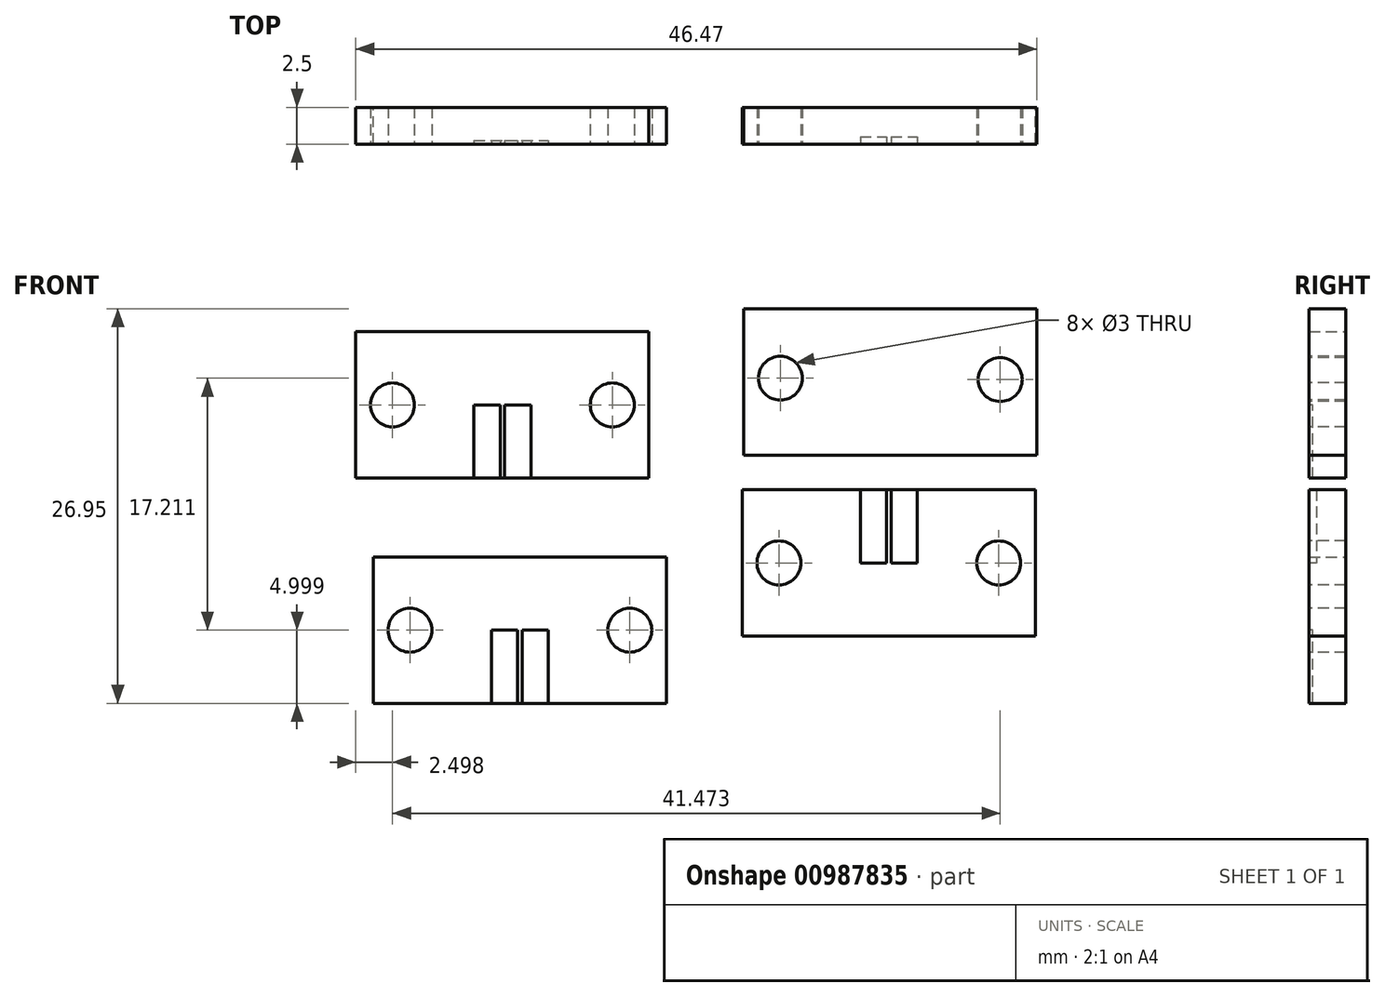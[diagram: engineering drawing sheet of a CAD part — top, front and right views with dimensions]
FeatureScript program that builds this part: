
annotation { "Feature Type Name" : "Feature", "Feature Type Description" : "" }
export const myFeature = defineFeature(function(context is Context, id is Id, definition is map)
    precondition{}
    {
        {
            var Q0;
            Q0=qCreatedBy(makeId("Front.planeOp"),FACE);
            var sketch = newSketch(context, id + "F0", { "sketchPlane" : qUnion([Q0])});
            skLineSegment(sketch, "E0.bottom", {"start": v(-45.26, 43.67) * mm, "end": v(-25.26, 43.67) * mm});
            skLineSegment(sketch, "E0.top", {"start": v(-45.26, 33.67) * mm, "end": v(-25.26, 33.67) * mm});
            skLineSegment(sketch, "E0.left", {"start": v(-45.26, 43.67) * mm, "end": v(-45.26, 33.67) * mm});
            skLineSegment(sketch, "E0.right", {"start": v(-25.26, 43.67) * mm, "end": v(-25.26, 33.67) * mm});
            skLineSegment(sketch, "E1.bottom", {"start": v(-45.36, 31.31) * mm, "end": v(-25.36, 31.31) * mm});
            skLineSegment(sketch, "E1.top", {"start": v(-45.36, 21.31) * mm, "end": v(-25.36, 21.31) * mm});
            skLineSegment(sketch, "E1.left", {"start": v(-45.36, 31.31) * mm, "end": v(-45.36, 21.31) * mm});
            skLineSegment(sketch, "E1.right", {"start": v(-25.36, 31.31) * mm, "end": v(-25.36, 21.31) * mm});
            skSolve(sketch);
        }
        {
            var Q0;
            Q0 = qSketchRegion(id + "F0", true);
            extrude(context, id + "F1", {"entities" : qUnion([Q0]), "depth" : 2.5 * mm, "offsetDistance" : 25 * mm});
        }
        {
            var Q0;
            Q0=makeQuery(id+"F1.opExtrude","CAP_FACE",FACE,{"disambiguationData":[OSD([sQuery(id+"F0.wireOp",EDGE,"E1.bottom"),sQuery(id+"F0.wireOp",EDGE,"E1.top"),sQuery(id+"F0.wireOp",EDGE,"E1.left"),sQuery(id+"F0.wireOp",EDGE,"E1.right")])],"isStart":false});
            var sketch = newSketch(context, id + "F2", { "sketchPlane" : qUnion([Q0])});
            skPoint(sketch, "E2", {"position": v(-35.36, 26.31) * mm});
            skLineSegment(sketch, "E3.bottom", {"start": v(-37.3, 31.9) * mm, "end": v(-35.5, 31.9) * mm});
            skLineSegment(sketch, "E3.top", {"start": v(-37.3, 26.31) * mm, "end": v(-35.5, 26.31) * mm});
            skLineSegment(sketch, "E3.left", {"start": v(-37.3, 31.9) * mm, "end": v(-37.3, 26.31) * mm});
            skLineSegment(sketch, "E3.right", {"start": v(-35.5, 31.9) * mm, "end": v(-35.5, 26.31) * mm});
            skLineSegment(sketch, "E4.bottom", {"start": v(-35.2, 32.08) * mm, "end": v(-33.4, 32.08) * mm});
            skLineSegment(sketch, "E4.top", {"start": v(-35.2, 26.31) * mm, "end": v(-33.4, 26.31) * mm});
            skLineSegment(sketch, "E4.left", {"start": v(-35.2, 32.08) * mm, "end": v(-35.2, 26.31) * mm});
            skLineSegment(sketch, "E4.right", {"start": v(-33.4, 32.08) * mm, "end": v(-33.4, 26.31) * mm});
            skSolve(sketch);
        }
        {
            var Q0;
            Q0 = qSketchRegion(id + "F2", true);
            extrude(context, id + "F3", {"entities" : qUnion([Q0]), "operationType" : NewBodyOperationType.REMOVE, "oppositeDirection" : true, "depth" : .5 * mm, "offsetDistance" : 25 * mm});
        }
        {
            var Q0;
            Q0=makeQuery(id+"F1.opExtrude","CAP_FACE",FACE,{"disambiguationData":[OSD([sQuery(id+"F0.wireOp",EDGE,"E1.bottom"),sQuery(id+"F0.wireOp",EDGE,"E1.top"),sQuery(id+"F0.wireOp",EDGE,"E1.left"),sQuery(id+"F0.wireOp",EDGE,"E1.right")])],"isStart":false});
            var sketch = newSketch(context, id + "F4", { "sketchPlane" : qUnion([Q0])});
            skPoint(sketch, "E5", {"position": v(-42.86, 26.31) * mm});
            skPoint(sketch, "E6", {"position": v(-27.86, 26.31) * mm});
            skCircle(sketch, "E7", {"center": v(-42.86, 26.31) * mm, "radius": 1.5 * mm});
            skCircle(sketch, "E8", {"center": v(-27.86, 26.31) * mm, "radius": 1.5 * mm});
            skSolve(sketch);
        }
        {
            var Q0;
            Q0 = qSketchRegion(id + "F4", true);
            extrude(context, id + "F5", {"entities" : qUnion([Q0]), "operationType" : NewBodyOperationType.REMOVE, "oppositeDirection" : true, "depth" : 3 * mm, "offsetDistance" : 25 * mm});
        }
        {
            var Q0;
            Q0=makeQuery(id+"F1.opExtrude","CAP_FACE",FACE,{"disambiguationData":[OSD([sQuery(id+"F0.wireOp",EDGE,"E0.bottom"),sQuery(id+"F0.wireOp",EDGE,"E0.top"),sQuery(id+"F0.wireOp",EDGE,"E0.left"),sQuery(id+"F0.wireOp",EDGE,"E0.right")])],"isStart":false});
            var sketch = newSketch(context, id + "F6", { "sketchPlane" : qUnion([Q0])});
            skPoint(sketch, "E9", {"position": v(-42.76, 38.93) * mm});
            skPoint(sketch, "E10", {"position": v(-27.76, 38.83) * mm});
            skCircle(sketch, "E11", {"center": v(-42.76, 38.93) * mm, "radius": 1.5 * mm});
            skCircle(sketch, "E12", {"center": v(-27.76, 38.83) * mm, "radius": 1.5 * mm});
            skSolve(sketch);
        }
        {
            var Q0;
            Q0 = qSketchRegion(id + "F6", true);
            extrude(context, id + "F7", {"entities" : qUnion([Q0]), "operationType" : NewBodyOperationType.REMOVE, "oppositeDirection" : true, "depth" : 3 * mm, "offsetDistance" : 25 * mm});
        }
        {
            var Q0;
            Q0=qCreatedBy(makeId("Front.planeOp"),FACE);
            var sketch = newSketch(context, id + "F8", { "sketchPlane" : qUnion([Q0])});
            skLineSegment(sketch, "E13.bottom", {"start": v(-71.73, 42.1) * mm, "end": v(-51.73, 42.1) * mm});
            skLineSegment(sketch, "E13.top", {"start": v(-71.73, 32.1) * mm, "end": v(-51.73, 32.1) * mm});
            skLineSegment(sketch, "E13.left", {"start": v(-71.73, 42.1) * mm, "end": v(-71.73, 32.1) * mm});
            skLineSegment(sketch, "E13.right", {"start": v(-51.73, 42.1) * mm, "end": v(-51.73, 32.1) * mm});
            skLineSegment(sketch, "E14.bottom", {"start": v(-70.54, 26.72) * mm, "end": v(-50.54, 26.72) * mm});
            skLineSegment(sketch, "E14.top", {"start": v(-70.54, 16.72) * mm, "end": v(-50.54, 16.72) * mm});
            skLineSegment(sketch, "E14.left", {"start": v(-70.54, 26.72) * mm, "end": v(-70.54, 16.72) * mm});
            skLineSegment(sketch, "E14.right", {"start": v(-50.54, 26.72) * mm, "end": v(-50.54, 16.72) * mm});
            skSolve(sketch);
        }
        {
            var Q0;
            Q0 = qSketchRegion(id + "F8", true);
            extrude(context, id + "F9", {"entities" : qUnion([Q0]), "depth" : 2.5 * mm, "offsetDistance" : 25 * mm});
        }
        {
            var Q0;
            Q0=makeQuery(id+"F9.opExtrude","CAP_FACE",FACE,{"disambiguationData":[OSD([sQuery(id+"F8.wireOp",EDGE,"E13.bottom"),sQuery(id+"F8.wireOp",EDGE,"E13.top"),sQuery(id+"F8.wireOp",EDGE,"E13.left"),sQuery(id+"F8.wireOp",EDGE,"E13.right")])],"isStart":false});
            var sketch = newSketch(context, id + "F10", { "sketchPlane" : qUnion([Q0])});
            skLineSegment(sketch, "E15.bottom", {"start": v(-63.68, 32.1) * mm, "end": v(-61.88, 32.1) * mm});
            skLineSegment(sketch, "E15.top", {"start": v(-63.68, 37.1) * mm, "end": v(-61.88, 37.1) * mm});
            skLineSegment(sketch, "E15.left", {"start": v(-63.68, 32.1) * mm, "end": v(-63.68, 37.1) * mm});
            skLineSegment(sketch, "E15.right", {"start": v(-61.88, 32.1) * mm, "end": v(-61.88, 37.1) * mm});
            skLineSegment(sketch, "E16.bottom", {"start": v(-59.78, 32.1) * mm, "end": v(-61.58, 32.1) * mm});
            skLineSegment(sketch, "E16.top", {"start": v(-59.78, 37.1) * mm, "end": v(-61.58, 37.1) * mm});
            skLineSegment(sketch, "E16.left", {"start": v(-59.78, 32.1) * mm, "end": v(-59.78, 37.1) * mm});
            skLineSegment(sketch, "E16.right", {"start": v(-61.58, 32.1) * mm, "end": v(-61.58, 37.1) * mm});
            skPoint(sketch, "E17", {"position": v(-61.73, 37.1) * mm});
            skSolve(sketch);
        }
        {
            var Q0;
            Q0 = qSketchRegion(id + "F10", true);
            extrude(context, id + "F11", {"entities" : qUnion([Q0]), "operationType" : NewBodyOperationType.REMOVE, "oppositeDirection" : true, "depth" : .25 * mm, "offsetDistance" : 25 * mm});
        }
        {
            var Q0;
            Q0=makeQuery(id+"F9.opExtrude","CAP_FACE",FACE,{"disambiguationData":[OSD([sQuery(id+"F8.wireOp",EDGE,"E14.bottom"),sQuery(id+"F8.wireOp",EDGE,"E14.top"),sQuery(id+"F8.wireOp",EDGE,"E14.left"),sQuery(id+"F8.wireOp",EDGE,"E14.right")])],"isStart":false});
            var sketch = newSketch(context, id + "F12", { "sketchPlane" : qUnion([Q0])});
            skLineSegment(sketch, "E18.bottom", {"start": v(-62.49, 16.72) * mm, "end": v(-60.69, 16.72) * mm});
            skLineSegment(sketch, "E18.top", {"start": v(-62.49, 21.72) * mm, "end": v(-60.69, 21.72) * mm});
            skLineSegment(sketch, "E18.left", {"start": v(-62.49, 16.72) * mm, "end": v(-62.49, 21.72) * mm});
            skLineSegment(sketch, "E18.right", {"start": v(-60.69, 16.72) * mm, "end": v(-60.69, 21.72) * mm});
            skLineSegment(sketch, "E19.bottom", {"start": v(-60.39, 16.72) * mm, "end": v(-58.59, 16.72) * mm});
            skLineSegment(sketch, "E19.top", {"start": v(-60.39, 21.72) * mm, "end": v(-58.59, 21.72) * mm});
            skLineSegment(sketch, "E19.left", {"start": v(-60.39, 16.72) * mm, "end": v(-60.39, 21.72) * mm});
            skLineSegment(sketch, "E19.right", {"start": v(-58.59, 16.72) * mm, "end": v(-58.59, 21.72) * mm});
            skPoint(sketch, "E20", {"position": v(-60.54, 21.72) * mm});
            skSolve(sketch);
        }
        {
            var Q0;
            Q0 = qSketchRegion(id + "F12", true);
            extrude(context, id + "F13", {"entities" : qUnion([Q0]), "operationType" : NewBodyOperationType.REMOVE, "oppositeDirection" : true, "depth" : .25 * mm, "offsetDistance" : 25 * mm});
        }
        {
            var Q0;
            Q0=makeQuery(id+"F9.opExtrude","CAP_FACE",FACE,{"disambiguationData":[OSD([sQuery(id+"F8.wireOp",EDGE,"E13.bottom"),sQuery(id+"F8.wireOp",EDGE,"E13.top"),sQuery(id+"F8.wireOp",EDGE,"E13.left"),sQuery(id+"F8.wireOp",EDGE,"E13.right")])],"isStart":false});
            var sketch = newSketch(context, id + "F14", { "sketchPlane" : qUnion([Q0])});
            skPoint(sketch, "E21", {"position": v(-69.23, 37.1) * mm});
            skPoint(sketch, "E22", {"position": v(-54.23, 37.1) * mm});
            skCircle(sketch, "E23", {"center": v(-69.23, 37.1) * mm, "radius": 1.5 * mm});
            skCircle(sketch, "E24", {"center": v(-54.23, 37.1) * mm, "radius": 1.5 * mm});
            skSolve(sketch);
        }
        {
            var Q0;
            Q0 = qSketchRegion(id + "F14", true);
            extrude(context, id + "F15", {"entities" : qUnion([Q0]), "operationType" : NewBodyOperationType.REMOVE, "oppositeDirection" : true, "depth" : 3 * mm, "offsetDistance" : 25 * mm});
        }
        {
            var Q0;
            Q0=makeQuery(id+"F9.opExtrude","CAP_FACE",FACE,{"disambiguationData":[OSD([sQuery(id+"F8.wireOp",EDGE,"E14.bottom"),sQuery(id+"F8.wireOp",EDGE,"E14.top"),sQuery(id+"F8.wireOp",EDGE,"E14.left"),sQuery(id+"F8.wireOp",EDGE,"E14.right")])],"isStart":false});
            var sketch = newSketch(context, id + "F16", { "sketchPlane" : qUnion([Q0])});
            skPoint(sketch, "E25", {"position": v(-68.04, 21.72) * mm});
            skPoint(sketch, "E26", {"position": v(-53.04, 21.72) * mm});
            skCircle(sketch, "E27", {"center": v(-68.04, 21.72) * mm, "radius": 1.5 * mm});
            skCircle(sketch, "E28", {"center": v(-53.04, 21.72) * mm, "radius": 1.5 * mm});
            skSolve(sketch);
        }
        {
            var Q0;
            Q0 = qSketchRegion(id + "F16", true);
            extrude(context, id + "F17", {"entities" : qUnion([Q0]), "operationType" : NewBodyOperationType.REMOVE, "oppositeDirection" : true, "depth" : 3 * mm, "offsetDistance" : 25 * mm});
        }
    });
